# Revit family: KEUCO_14919010000
name_source: partatom
category: Allgemeines Modell
revit_build: Autodesk Revit 2016 (Build: 20150220_1215(x64)
units: mm (PartAtom-declared; Revit-internal decimal feet)

## family parameters
Arbeitsebenenbasiert = Ja
Beim Laden mit Abzugskörper schneiden = Nein
Bemaßung runder Anschluss = Durchmesser verwenden
Gemeinsam genutzt = Nein
Immer vertikal = Nein
Kann Basisbauteil für Bewehrung sein = Nein
Raumberechnungspunkt = Nein
Teiletyp = Normal

## types (3) — shared parameters
Hersteller = KEUCO
Rail Length = 851 mm
Serie = Plan
URL = https://www.keuco.com
Verwendung = GWC / WP
Vorgabe-Ansicht = 1219 mm
zero-valued in all types: Gewicht

## per-type parameters (varying)
| type | Ausschreibungstext | Material |
| 14919010000 | KEUCO PLAN Handtuchhalter 14919010000
Hochglanzverchromter Handtuchhalter 
in ästhetischem, funktionalem Design
zwei übereinander angeordnete, 
unabhängig voneinander seitlich schwenkbare Haltearme, 
antistatisch, leicht zu reinigen
Höhe 69 mm, Ausladung 300 mm
Der Handtuchhalter wird verdeckt angebracht
Lieferung inkl. korrosionsfreiem Befestigungsmaterial | Verchromt |
| 14919070000 | KEUCO PLAN Handtuchhalter 14919070000
Handtuchhalter aus hochwertigem Edelstahl 
in ästhetischem, funktionalem Design,
zwei übereinander angeordnete, 
unabhängig voneinander seitlich schwenkbare Haltearme, 
antistatisch, leicht zu reinigen
Höhe 69 mm, Ausladung 300 mm
Der Handtuchhalter wird verdeckt angebracht
Lieferung inkl. korrosionsfreiem Befestigungsmaterial | Verchromt |
| 14919170000 | KEUCO PLAN Handtuchhalter 14919170000
Handtuchhalter aus silber-eloxiertem Aluminium (E6 EV1)/verchromt 
in ästhetischem, funktionalem Design,
zwei übereinander angeordnete, 
unabhängig voneinander seitlich schwenkbare Haltearme, 
antistatisch, leicht zu reinigen
Die Wandhalterung ist als Design-Element hochglanzverchromt
Höhe 69 mm, Ausladung 300 mm
Der Handtuchhalter wird verdeckt angebracht
Lieferung inkl. korrosionsfreiem Befestigungsmaterial | Aluminium 1100-H18 |

note: column(s) folded — value = type name in every type: Artikelnummer

## geometry (parser evidence)
native form markers: Blend x4, Sweep x2
no freeform markers — native parametric forms only
